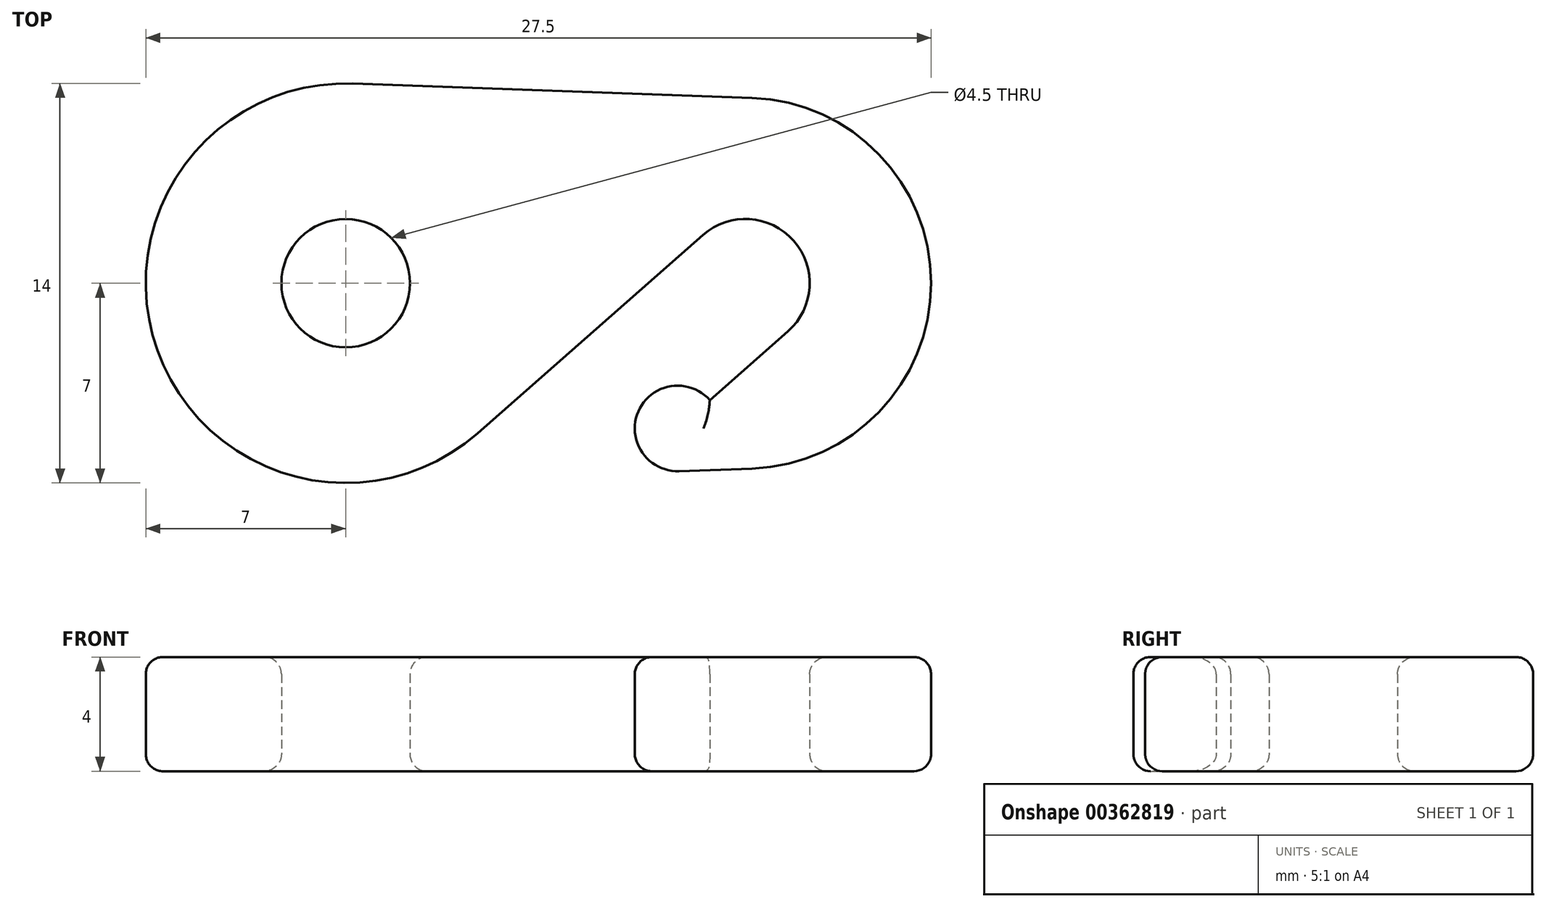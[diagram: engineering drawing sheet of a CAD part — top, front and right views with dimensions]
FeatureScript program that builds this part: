
annotation { "Feature Type Name" : "Feature", "Feature Type Description" : "" }
export const myFeature = defineFeature(function(context is Context, id is Id, definition is map)
    precondition{}
    {
        {
            var Q0;
            Q0=qCreatedBy(makeId("Top.planeOp"),FACE);
            var sketch = newSketch(context, id + "F0", { "sketchPlane" : qUnion([Q0])});
            skCircle(sketch, "E0", {"center": v(0, 0) * mm, "radius": 7 * mm});
            skCircle(sketch, "E1", {"center": v(0, 0) * mm, "radius": 2.25 * mm});
            skCircle(sketch, "E2", {"center": v(14, 0) * mm, "radius": 6.5 * mm});
            skCircle(sketch, "E3", {"center": v(14, 0) * mm, "radius": 2.25 * mm});
            skLineSegment(sketch, "E4", {"start": v(4.63, -5.25) * mm, "end": v(12.51, 1.69) * mm});
            skLineSegment(sketch, "E5", {"start": v(0.25, 7) * mm, "end": v(14.23, 6.5) * mm});
            skLineSegment(sketch, "E6", {"start": v(0.25, -7) * mm, "end": v(14.23, -6.5) * mm});
            skLineSegment(sketch, "E7", {"start": v(15.49, -1.69) * mm, "end": v(9.85, -6.65) * mm});
            skCircle(sketch, "E8", {"center": v(11.62, -5.09) * mm, "radius": 1.5 * mm});
            skSolve(sketch);
        }
        {
            var Q0;
            Q0=makeQuery(id+"F0.imprint","IMPRINT",FACE,{"disambiguationData":[TD([[makeQuery(id+"F0.imprint","IMPRINT",EDGE,{"derivedFrom":sQuery(id+"F0.wireOp",EDGE,"E1")}),-1.0]])]});
            var Q1;
            {var subQ3=sQuery(id+"F0.wireOp",EDGE,"E5");Q1=makeQuery(id+"F0.imprint","IMPRINT",FACE,{"disambiguationData":[TD([[makeQuery(id+"F0.imprint","IMPRINT",EDGE,{"derivedFrom":subQ3}),-1.0]])]});}
            var Q2;
            {var subQ5=sQuery(id+"F0.wireOp",EDGE,"E2");var subQ9=makeQuery(id+"F0.imprint","INTERSECT",VERTEX,{"derivedFrom":[subQ5,sQuery(id+"F0.wireOp",EDGE,"E5")]});Q2=makeQuery(id+"F0.imprint","IMPRINT",FACE,{"disambiguationData":[TD([[makeQuery(id+"F0.imprint","IMPRINT",EDGE,{"disambiguationData":[TD([[subQ9,-1.0]])],"derivedFrom":subQ5}),1.0]])]});}
            var Q3;
            {var subQ0=sQuery(id+"F0.wireOp",EDGE,"E8");var subQ1=sQuery(id+"F0.wireOp",EDGE,"E2");var subQ2=makeQuery(id+"F0.imprint","INTERSECT",VERTEX,{"disambiguationData":[OD(0.0)],"derivedFrom":[subQ1,subQ0]});Q3=makeQuery(id+"F0.imprint","IMPRINT",FACE,{"disambiguationData":[TD([[makeQuery(id+"F0.imprint","IMPRINT",EDGE,{"disambiguationData":[TD([[subQ2,-1.0]])],"derivedFrom":subQ1}),1.0]])]});}
            var Q4;
            {var subQ0=sQuery(id+"F0.wireOp",EDGE,"E8");var subQ1=sQuery(id+"F0.wireOp",EDGE,"E2");var subQ2=makeQuery(id+"F0.imprint","INTERSECT",VERTEX,{"disambiguationData":[OD(0.0)],"derivedFrom":[subQ1,subQ0]});Q4=makeQuery(id+"F0.imprint","IMPRINT",FACE,{"disambiguationData":[TD([[makeQuery(id+"F0.imprint","IMPRINT",EDGE,{"disambiguationData":[TD([[subQ2,-1.0]])],"derivedFrom":subQ1}),-1.0]])]});}
            var Q5;
            {var subQ0=sQuery(id+"F0.wireOp",EDGE,"E7");var subQ1=sQuery(id+"F0.wireOp",EDGE,"E2");var subQ2=makeQuery(id+"F0.imprint","INTERSECT",VERTEX,{"derivedFrom":[subQ1,subQ0]});Q5=makeQuery(id+"F0.imprint","IMPRINT",FACE,{"disambiguationData":[TD([[makeQuery(id+"F0.imprint","IMPRINT",EDGE,{"disambiguationData":[TD([[subQ2,-1.0]])],"derivedFrom":subQ1}),-1.0]])]});}
            var Q6;
            {var subQ0=sQuery(id+"F0.wireOp",EDGE,"E7");var subQ1=sQuery(id+"F0.wireOp",EDGE,"E2");var subQ2=makeQuery(id+"F0.imprint","INTERSECT",VERTEX,{"derivedFrom":[subQ1,subQ0]});Q6=makeQuery(id+"F0.imprint","IMPRINT",FACE,{"disambiguationData":[TD([[makeQuery(id+"F0.imprint","IMPRINT",EDGE,{"disambiguationData":[TD([[subQ2,-1.0]])],"derivedFrom":subQ1}),1.0]])]});}
            var Q7;
            {var subQ0=sQuery(id+"F0.wireOp",EDGE,"E6");var subQ1=sQuery(id+"F0.wireOp",EDGE,"E2");var subQ2=makeQuery(id+"F0.imprint","INTERSECT",VERTEX,{"derivedFrom":[subQ1,subQ0]});Q7=makeQuery(id+"F0.imprint","IMPRINT",FACE,{"disambiguationData":[TD([[makeQuery(id+"F0.imprint","IMPRINT",EDGE,{"disambiguationData":[TD([[subQ2,1.0]])],"derivedFrom":subQ1}),-1.0]])]});}
            var Q8;
            {var subQ0=sQuery(id+"F0.wireOp",EDGE,"E4");var subQ1=sQuery(id+"F0.wireOp",EDGE,"E0");var subQ2=makeQuery(id+"F0.imprint","INTERSECT",VERTEX,{"derivedFrom":[subQ1,subQ0]});Q8=makeQuery(id+"F0.imprint","IMPRINT",FACE,{"disambiguationData":[TD([[makeQuery(id+"F0.imprint","IMPRINT",EDGE,{"disambiguationData":[TD([[subQ2,-1.0]])],"derivedFrom":subQ1}),-1.0]])]});}
            extrude(context, id + "F1", {"entities" : qUnion([Q0, Q1, Q2, Q3, Q4, Q5, Q6, Q7, Q8]), "depth" : 4 * mm});
        }
        {
            var Q0;
            Q0=makeQuery(id+"F1.opExtrude","CAP_FACE",FACE,{"disambiguationData":[OSD([sQuery(id+"F0.wireOp",EDGE,"E0"),sQuery(id+"F0.wireOp",EDGE,"E1"),sQuery(id+"F0.wireOp",EDGE,"E2"),sQuery(id+"F0.wireOp",EDGE,"E3"),sQuery(id+"F0.wireOp",EDGE,"E4"),sQuery(id+"F0.wireOp",EDGE,"E5"),sQuery(id+"F0.wireOp",EDGE,"E6"),sQuery(id+"F0.wireOp",EDGE,"E7"),sQuery(id+"F0.wireOp",EDGE,"E8")])],"isStart":true});
            var Q1;
            Q1=makeQuery(id+"F1.opExtrude","CAP_FACE",FACE,{"disambiguationData":[OSD([sQuery(id+"F0.wireOp",EDGE,"E0"),sQuery(id+"F0.wireOp",EDGE,"E1"),sQuery(id+"F0.wireOp",EDGE,"E2"),sQuery(id+"F0.wireOp",EDGE,"E3"),sQuery(id+"F0.wireOp",EDGE,"E4"),sQuery(id+"F0.wireOp",EDGE,"E5"),sQuery(id+"F0.wireOp",EDGE,"E6"),sQuery(id+"F0.wireOp",EDGE,"E7"),sQuery(id+"F0.wireOp",EDGE,"E8")])],"isStart":false});
            fillet(context, id + "F2", {"entities" : qUnion([Q0, Q1]), "radius" : 0.6 * mm, "tangentPropagation" : true, "allowEdgeOverflow" : false});
        }
    });
